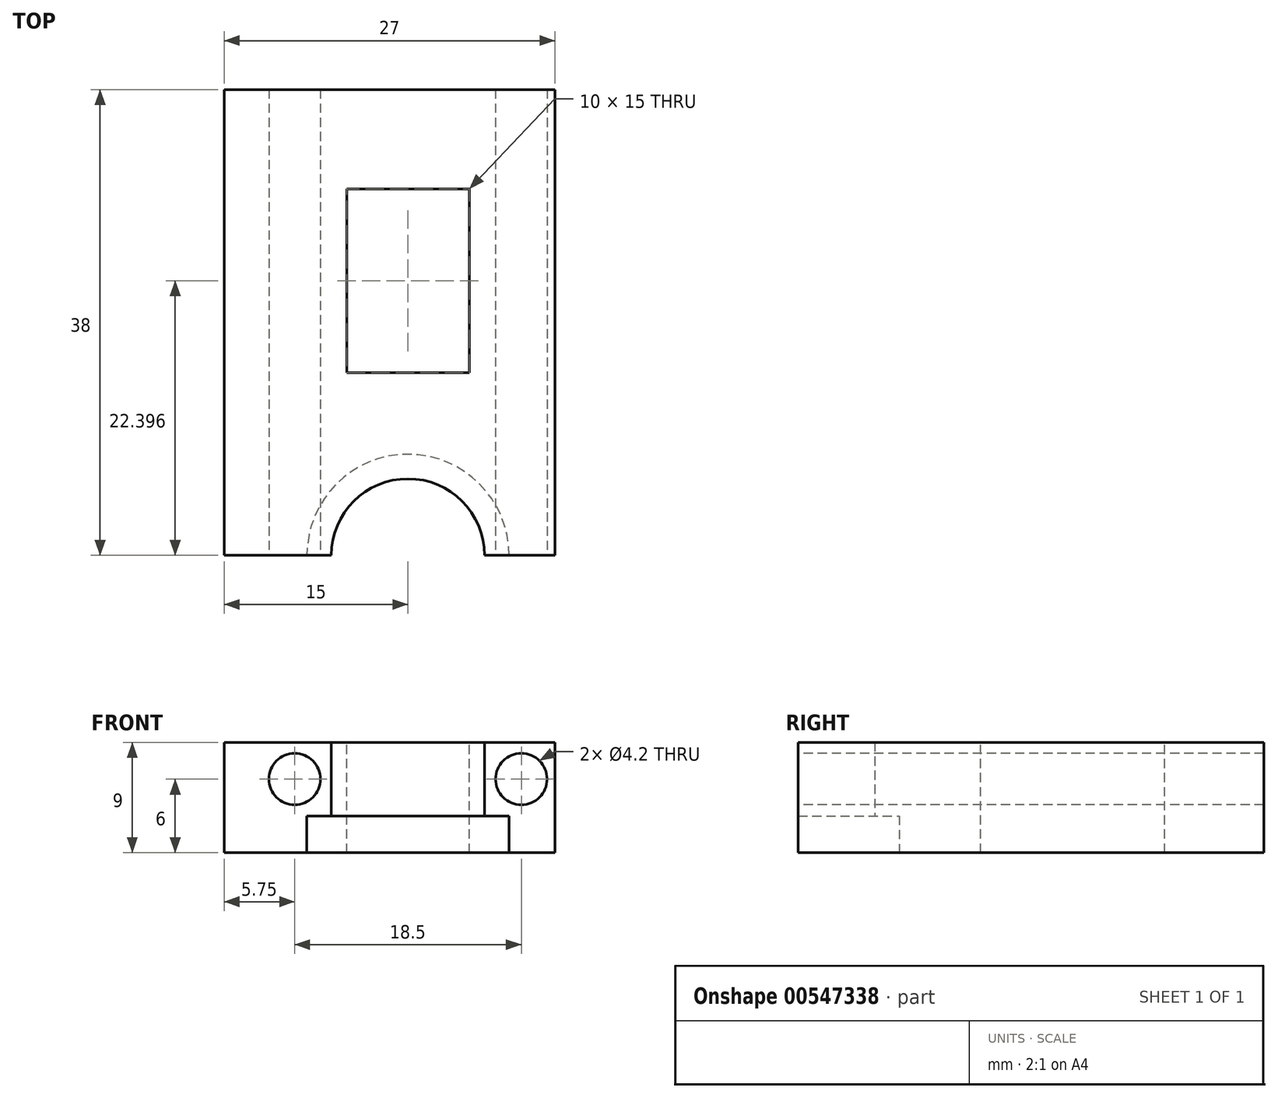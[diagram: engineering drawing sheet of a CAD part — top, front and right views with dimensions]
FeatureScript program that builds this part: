
annotation { "Feature Type Name" : "Feature", "Feature Type Description" : "" }
export const myFeature = defineFeature(function(context is Context, id is Id, definition is map)
    precondition{}
    {
        {
            var Q0;
            Q0=qCreatedBy(makeId("Top.planeOp"),FACE);
            var sketch = newSketch(context, id + "F0", { "sketchPlane" : qUnion([Q0])});
            skLineSegment(sketch, "E0.bottom", {"start": v(-15, 0) * mm, "end": v(-6.25, 0) * mm});
            skLineSegment(sketch, "E0.top", {"start": v(-15, 38) * mm, "end": v(12, 38) * mm});
            skLineSegment(sketch, "E0.left", {"start": v(-15, 0) * mm, "end": v(-15, 38) * mm});
            skLineSegment(sketch, "E0.right", {"start": v(12, 0) * mm, "end": v(12, 38) * mm});
            skArc(sketch, "E1", {"start": v(6.25, 0) * mm, "mid": v(0, 6.25) * mm, "end": v(-6.25, 0) * mm});
            skLineSegment(sketch, "E2.trimOffspring", {"start": v(6.25, 0) * mm, "end": v(12, 0) * mm});
            skSolve(sketch);
        }
        {
            var Q0;
            Q0 = qSketchRegion(id + "F0", true);
            extrude(context, id + "F1", {"entities" : qUnion([Q0]), "flatOperationType" : FlatOperationType.REMOVE, "depth" : 9 * mm, "offsetDistance" : 25 * mm, "domain" : OperationDomain.MODEL});
        }
        {
            var Q0;
            Q0=makeQuery(id+"F1.opExtrude","CAP_FACE",FACE,{"disambiguationData":[OSD([sQuery(id+"F0.wireOp",EDGE,"E0.bottom"),sQuery(id+"F0.wireOp",EDGE,"E0.top"),sQuery(id+"F0.wireOp",EDGE,"E0.left"),sQuery(id+"F0.wireOp",EDGE,"E0.right"),sQuery(id+"F0.wireOp",EDGE,"E1"),sQuery(id+"F0.wireOp",EDGE,"E2.trimOffspring")])],"isStart":true});
            var sketch = newSketch(context, id + "F2", { "sketchPlane" : qUnion([Q0])});
            skArc(sketch, "E3", {"start": v(-6.25, 0) * mm, "mid": v(0, -6.25) * mm, "end": v(6.25, 0) * mm});
            skArc(sketch, "E4", {"start": v(-8.25, 0) * mm, "mid": v(0, -8.25) * mm, "end": v(8.25, 0) * mm});
            skLineSegment(sketch, "E5", {"start": v(-6.25, 0) * mm, "end": v(-8.25, 0) * mm});
            skLineSegment(sketch, "E6", {"start": v(6.25, 0) * mm, "end": v(8.25, 0) * mm});
            skSolve(sketch);
        }
        {
            var Q0;
            Q0 = qSketchRegion(id + "F2", true);
            extrude(context, id + "F3", {"entities" : qUnion([Q0]), "operationType" : NewBodyOperationType.REMOVE, "flatOperationType" : FlatOperationType.REMOVE, "oppositeDirection" : true, "depth" : 3 * mm, "offsetDistance" : 25 * mm, "domain" : OperationDomain.MODEL});
        }
        {
            var Q0;
            Q0=qCreatedBy(makeId("Front.planeOp"),FACE);
            var sketch = newSketch(context, id + "F4", { "sketchPlane" : qUnion([Q0])});
            skCircle(sketch, "E7", {"center": v(-9.25, 6) * mm, "radius": 2.1 * mm});
            skCircle(sketch, "E8.MirrorC", {"center": v(9.25, 6) * mm, "radius": 2.1 * mm});
            skSolve(sketch);
        }
        {
            var Q0;
            Q0 = qSketchRegion(id + "F4", true);
            extrude(context, id + "F5", {"entities" : qUnion([Q0]), "operationType" : NewBodyOperationType.REMOVE, "endBound" : BoundingType.THROUGH_ALL, "oppositeDirection" : true, "depth" : 25 * mm, "offsetDistance" : 25 * mm});
        }
        {
            var Q0;
            Q0=makeQuery(id+"F1.opExtrude","CAP_FACE",FACE,{"disambiguationData":[OSD([sQuery(id+"F0.wireOp",EDGE,"E0.bottom"),sQuery(id+"F0.wireOp",EDGE,"E0.top"),sQuery(id+"F0.wireOp",EDGE,"E0.left"),sQuery(id+"F0.wireOp",EDGE,"E0.right"),sQuery(id+"F0.wireOp",EDGE,"E1"),sQuery(id+"F0.wireOp",EDGE,"E2.trimOffspring")])],"isStart":false});
            var sketch = newSketch(context, id + "F6", { "sketchPlane" : qUnion([Q0])});
            skLineSegment(sketch, "E9.bottom", {"start": v(-5, 29.9) * mm, "end": v(5, 29.9) * mm});
            skLineSegment(sketch, "E9.top", {"start": v(-5, 14.9) * mm, "end": v(5, 14.9) * mm});
            skLineSegment(sketch, "E9.left", {"start": v(-5, 29.9) * mm, "end": v(-5, 14.9) * mm});
            skLineSegment(sketch, "E9.right", {"start": v(5, 29.9) * mm, "end": v(5, 14.9) * mm});
            skPoint(sketch, "E9.middle", {"position": v(0, 22.4) * mm});
            skSolve(sketch);
        }
        {
            var Q0;
            Q0 = qSketchRegion(id + "F6", true);
            extrude(context, id + "F7", {"entities" : qUnion([Q0]), "operationType" : NewBodyOperationType.REMOVE, "endBound" : BoundingType.THROUGH_ALL, "oppositeDirection" : true, "depth" : 25 * mm, "offsetDistance" : 25 * mm});
        }
    });
